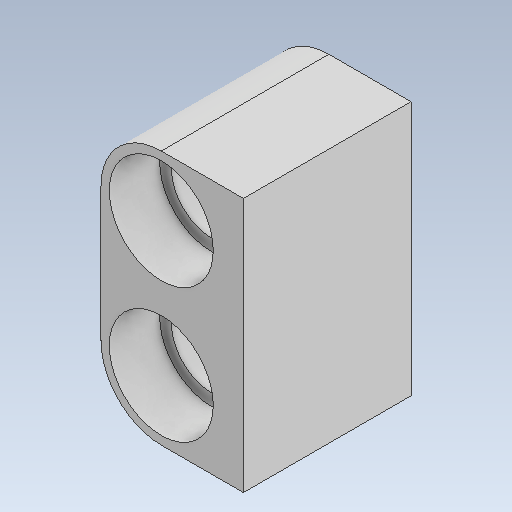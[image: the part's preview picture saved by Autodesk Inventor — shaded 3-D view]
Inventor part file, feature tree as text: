
AUTODESK INVENTOR PART (.ipt)
format: ipt  version: 2020 (Build 240168000, 168)  size: 138,240 bytes
history: native  units: mm
features: other x16, extrude x3, sketch x3
ambient origin geometry x8: Origin, YZ Plane, XZ Plane, XY Plane, X Axis, Y Axis, Z Axis, Center Point
bodies: Body1 (feature_tree)
feature tree (22):
  other  "Sólido1"
  extrude  "Extrusão1"  Depth=3.0mm TaperAngle=0.0deg
  extrude  "Extrusão2"  [1 undecoded]
  extrude  "Extrusão3"  [1 undecoded]
  sketch  "Esboço1"  dims[d0=10.0mm d1=0.0mm d2=3.0mm d3=0.0mm]
  other  "Referência1"
  other  "Referência2"
  other  "Referência3"
  other  "Referência4"
  sketch  "Esboço2"  dims[d4=1.0mm d5=0.0mm]
  other  "Referência5"
  other  "Referência6"
  sketch  "Esboço3"
  other  "Referência7"
  other  "Referência8"
  other  "<userpath>\Desktop\rabo\3d\ela.iam"
  other  "ela.iam"
  other  "viga_8:2"
  other  "pcb sensor de cor:1"
  other  "basesinha:1"
  other  "95658-EV3_Large_Motor v3_MIR:1"
  other  "10825-LtBluishGray_MIR:1"
note: 2 required parameter values undecoded (feature->parameter linkage not recoverable at this tier; creation-order binding heuristic only, values carry confidence <= 0.55)
